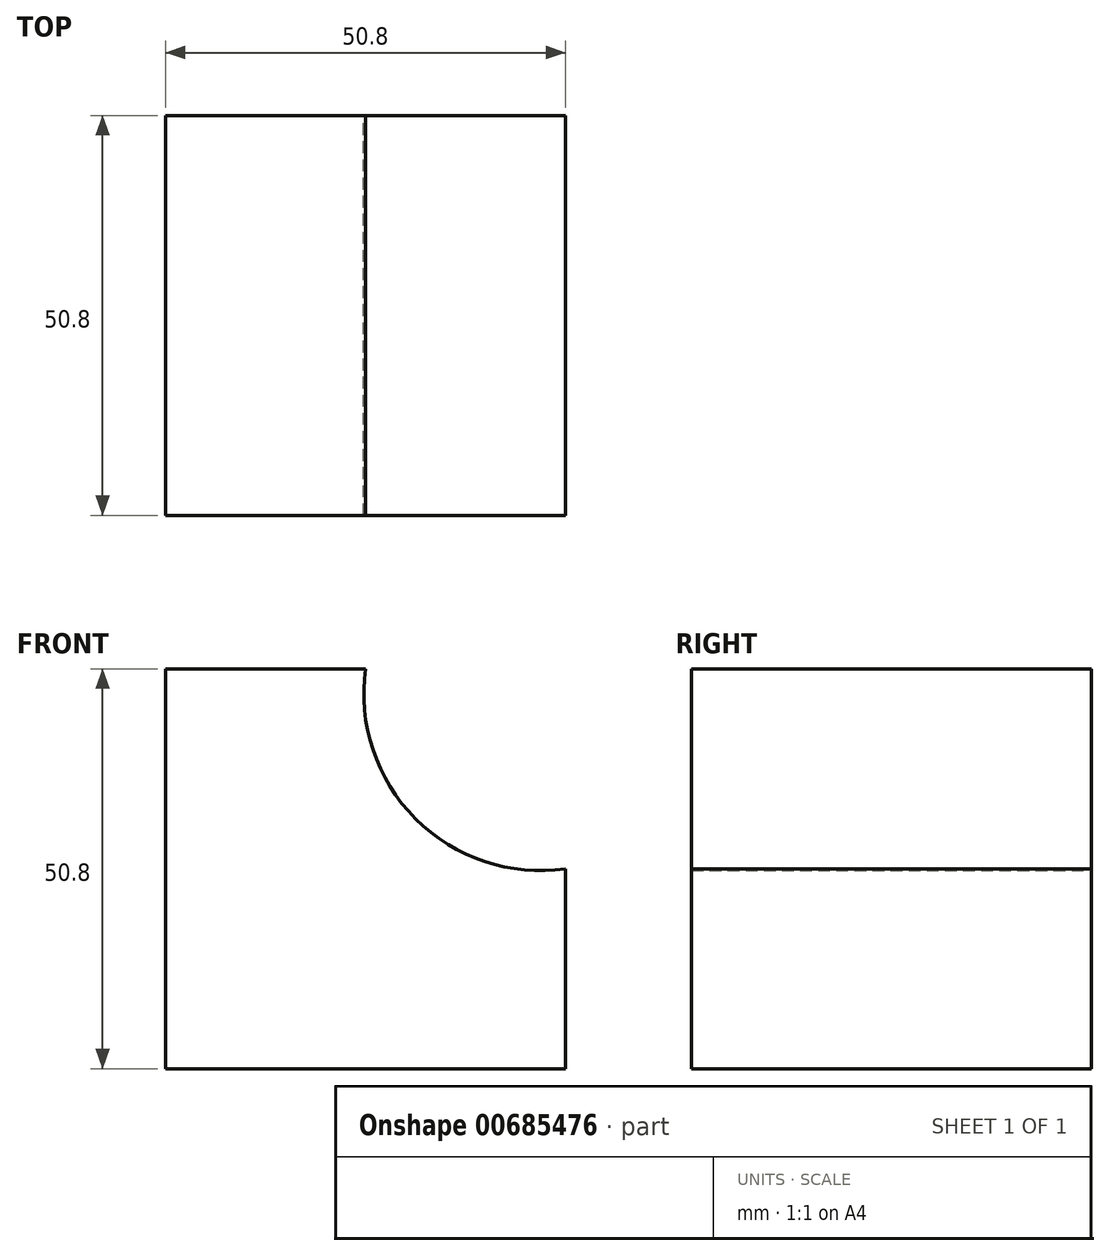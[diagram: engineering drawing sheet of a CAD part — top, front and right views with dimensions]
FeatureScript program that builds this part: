
annotation { "Feature Type Name" : "Feature", "Feature Type Description" : "" }
export const myFeature = defineFeature(function(context is Context, id is Id, definition is map)
    precondition{}
    {
        {
            var Q0;
            Q0=qCreatedBy(makeId("Front.planeOp"),FACE);
            var sketch = newSketch(context, id + "F0", { "sketchPlane" : qUnion([Q0])});
            skLineSegment(sketch, "E0", {"start": v(-42.68, 20.34) * mm, "end": v(-42.68, -30.46) * mm});
            skLineSegment(sketch, "E1", {"start": v(-42.68, -30.46) * mm, "end": v(8.12, -30.46) * mm});
            skLineSegment(sketch, "E2", {"start": v(8.12, -30.46) * mm, "end": v(8.12, -5.06) * mm});
            skLineSegment(sketch, "E3", {"start": v(-42.68, 20.34) * mm, "end": v(-17.28, 20.34) * mm});
            skArc(sketch, "E4", {"start": v(-17.28, 20.34) * mm, "mid": v(-10.93, 1.29) * mm, "end": v(8.12, -5.06) * mm});
            skSolve(sketch);
        }
        {
            var Q0;
            Q0=makeQuery(id+"F0.imprint","IMPRINT",FACE,{"disambiguationData":[TD([[makeQuery(id+"F0.imprint","IMPRINT",EDGE,{"derivedFrom":sQuery(id+"F0.wireOp",EDGE,"E0")}),1.0]])]});
            extrude(context, id + "F1", {"entities" : qUnion([Q0]), "depth" : 50.8 * mm, "offsetDistance" : 25.4 * mm});
        }
    });
